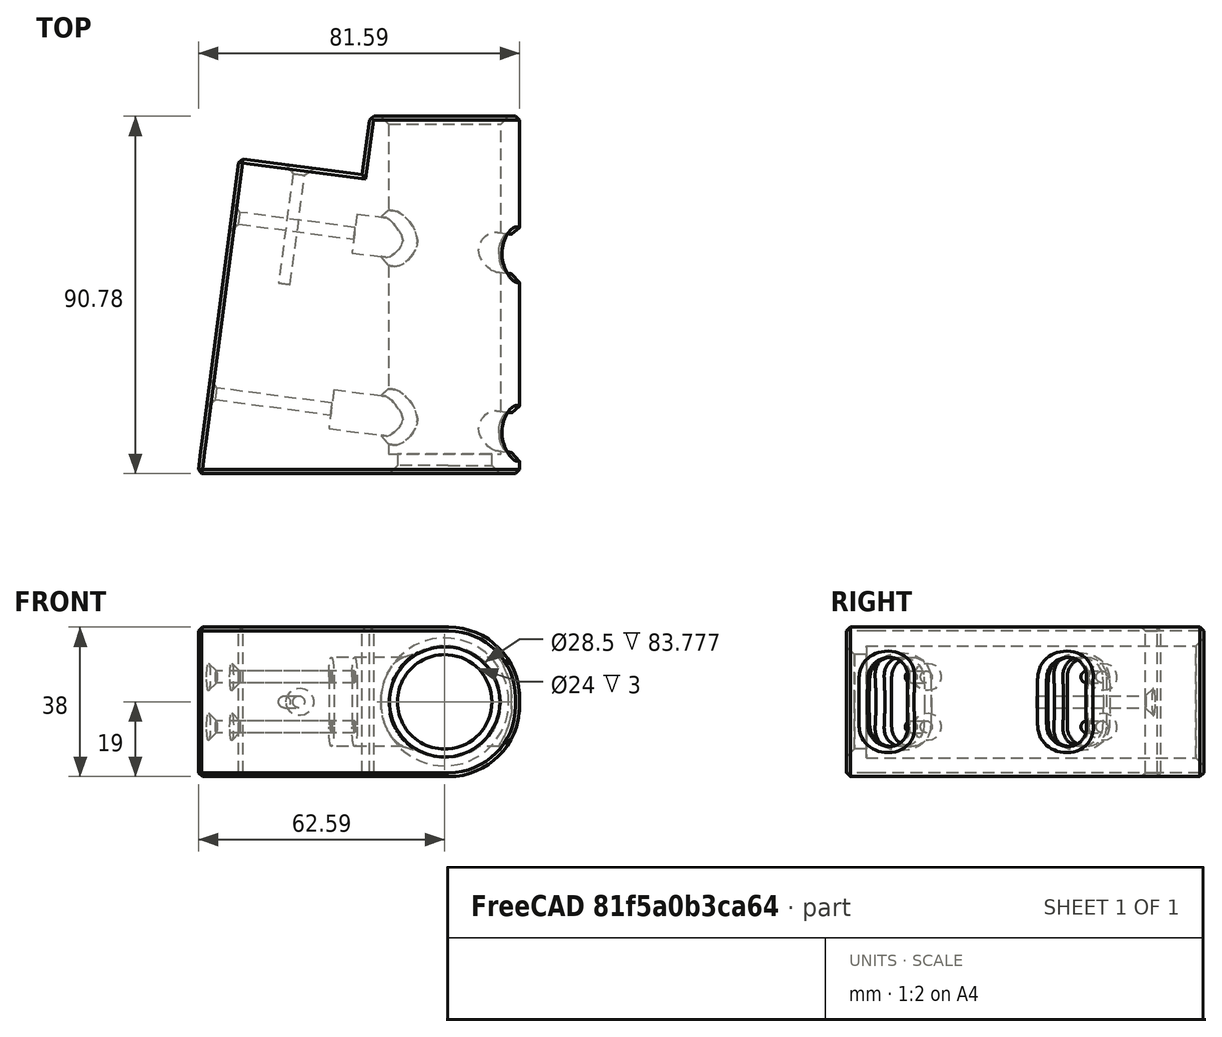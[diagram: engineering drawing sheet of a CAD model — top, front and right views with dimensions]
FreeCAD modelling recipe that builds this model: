
FCSTD DOCUMENT  (FreeCAD 0.18R16110 (Git))
Label: Support_mat_V2
License: All rights reserved
LicenseURL: http://en.wikipedia.org/wiki/All_rights_reserved
objects: PartDesign::Chamfer×9, Sketcher::SketchObject×8, PartDesign::Pocket×5, PartDesign::Pad×3, PartDesign::Fillet×1, PartDesign::Plane×1, PartDesign::Body×1, Mesh::Feature×1
note: 36 computed .brp shape members not serialized (recipe doc carries the construction recipe); baked Part::Feature solids carry a one-line shape summary decoded from their .brp

FEATURE [Sketcher::SketchObject] Sketch
  MapMode = 5
  Support = -> [XY_Plane]
  sketch-geometry (7):
    g0: LineSegment StartX=19 StartY=0 StartZ=0 EndX=-19 EndY=0 EndZ=0
    g1: LineSegment StartX=-61.9779 StartY=-85.1185 StartZ=0 EndX=-19 EndY=-90.7766 EndZ=0
    g2: LineSegment StartX=-19 StartY=-90.7766 StartZ=0 EndX=19 EndY=-90.7766 EndZ=0
    g3: LineSegment StartX=19 StartY=-90.7766 StartZ=0 EndX=19 EndY=0 EndZ=0
    g4: LineSegment StartX=-19 StartY=0 StartZ=0 EndX=-20.9579 EndY=-14.8717 EndZ=0
    g5: LineSegment StartX=-20.9579 StartY=-14.8717 StartZ=0 EndX=-52.1884 EndY=-10.7601 EndZ=0
    g6: LineSegment StartX=-52.1884 StartY=-10.7601 StartZ=0 EndX=-61.9779 EndY=-85.1185 EndZ=0
  constraints (20):
    c: PointOnObject(g0,g-1)
    c: Coincident(g1,g2)
    c: Horizontal(g2)
    c: Coincident(g2,g3)
    c: Coincident(g3,g0)
    c: Vertical(g3)
    c: Coincident(g0,g4)
    c: Coincident(g4,g5)
    c: Coincident(g5,g6)
    c: Coincident(g6,g1)
    c: Angle(g4,g0) = 1.7017
    c: Perpendicular(g4,g5)
    c: Perpendicular(g5,g6)
    c: Perpendicular(g1,g6)
    c: Distance(g5) = 31.5
    c: Distance(g4) = 15
    c: DistanceX(g0,g0) = 38
    c: Distance(g6) = 75
    c: Equal(g2,g0)
    c: Symmetric(g0,g0,g-2)
FEATURE [PartDesign::Pad] Pad
  Length = 38
  Length2 = 100
  Profile = -> Sketch
  Type = 0
FEATURE [Sketcher::SketchObject] Sketch001
  MapMode = 5
  Placement = pos=(0,0,0) rot=(0,0.707107,0.707107;3.14159rad)
  Support = -> [Pad]
  sketch-geometry (1):
    g0: Circle CenterX=0 CenterY=19 CenterZ=0 NormalX=0 NormalY=0 NormalZ=1 AngleXU=0 Radius=14.25
  constraints (3):
    c: Radius(g0) = 14.25
    c: Distance(g-1,g0) = 19
    c: PointOnObject(g0,g-2)
FEATURE [PartDesign::Pocket] Pocket
  BaseFeature = -> Pad
  Length = 100
  Length2 = 100
  Profile = -> Sketch001
  Type = 0
FEATURE [PartDesign::Fillet] Fillet
  Base = -> Pocket [Edge7,Edge8]
  BaseFeature = -> Pocket
  Radius = 18
FEATURE [Sketcher::SketchObject] Sketch002
  ExternalGeometry = -> [Fillet]
  MapMode = 5
  Placement = pos=(-49.9068,6.57036,0) rot=(-0.527011,0.600941,0.600941;4.11164rad)
  Support = -> [Fillet]
  sketch-geometry (4):
    g0: Circle CenterX=32.48 CenterY=25.3333 CenterZ=0 NormalX=0 NormalY=0 NormalZ=1 AngleXU=0 Radius=1.5
    g1: Circle CenterX=32.48 CenterY=12.6667 CenterZ=0 NormalX=0 NormalY=0 NormalZ=1 AngleXU=0 Radius=1.5
    g2: Circle CenterX=77.48 CenterY=25.3333 CenterZ=0 NormalX=0 NormalY=0 NormalZ=1 AngleXU=0 Radius=1.5
    g3: Circle CenterX=77.48 CenterY=12.6667 CenterZ=0 NormalX=0 NormalY=0 NormalZ=1 AngleXU=0 Radius=1.5
  constraints (12):
    c: Radius(g3) = 1.5
    c: Equal(g3,g2)
    c: Equal(g3,g0)
    c: Equal(g3,g1)
    c: Distance(g0,g-3) = 15
    c: Distance(g1,g-3) = 15
    c: Distance(g2,g-5) = 15
    c: Distance(g3,g-5) = 15
    c: DistanceY(g-1,g1) = 12.6667
    c: Distance(g0,g-4) = 12.6667
    c: Distance(g2,g-4) = 12.6667
    c: DistanceY(g-1,g3) = 12.6667
FEATURE [PartDesign::Pocket] Pocket001
  BaseFeature = -> Fillet
  Length = 100
  Length2 = 100
  Profile = -> Sketch002
  Type = 0
FEATURE [PartDesign::Plane] DatumPlane
  Length = 125.134
  MapMode = 5
  Placement = pos=(-18.6763,2.45878,0) rot=(-0.527011,0.600941,0.600941;4.11164rad)
  ResizeMode = 0
  Support = -> [Pocket001]
  Width = 62.57
FEATURE [Sketcher::SketchObject] Sketch003
  ExternalGeometry = -> [Pocket001]
  MapMode = 5
  Placement = pos=(-18.6763,2.45878,0) rot=(-0.527011,0.600941,0.600941;4.11164rad)
  Support = -> [DatumPlane]
  sketch-geometry (8):
    g0: ArcOfCircle CenterX=32.48 CenterY=25.3333 CenterZ=0 NormalX=0 NormalY=0 NormalZ=1 AngleXU=0 Radius=5 StartAngle=1.1e-15 EndAngle=3.14159
    g1: ArcOfCircle CenterX=32.48 CenterY=12.6667 CenterZ=0 NormalX=0 NormalY=0 NormalZ=1 AngleXU=0 Radius=5 StartAngle=3.14159 EndAngle=6.28319
    g2: LineSegment StartX=27.48 StartY=25.3333 StartZ=0 EndX=27.48 EndY=12.6667 EndZ=0
    g3: LineSegment StartX=37.48 StartY=25.3333 StartZ=0 EndX=37.48 EndY=12.6667 EndZ=0
    g4: ArcOfCircle CenterX=77.48 CenterY=25.3333 CenterZ=0 NormalX=0 NormalY=0 NormalZ=1 AngleXU=0 Radius=5 StartAngle=0 EndAngle=3.14159
    g5: ArcOfCircle CenterX=77.48 CenterY=12.6667 CenterZ=0 NormalX=0 NormalY=0 NormalZ=1 AngleXU=0 Radius=5 StartAngle=3.14159 EndAngle=6.28319
    g6: LineSegment StartX=72.48 StartY=25.3333 StartZ=0 EndX=72.48 EndY=12.6667 EndZ=0
    g7: LineSegment StartX=82.48 StartY=25.3333 StartZ=0 EndX=82.48 EndY=12.6667 EndZ=0
  constraints (16):
    c: Tangent(g0,g3) = 1.5708
    c: Tangent(g0,g2) = -1.5708
    c: Tangent(g2,g1) = -1.5708
    c: Tangent(g3,g1) = 1.5708
    c: Vertical(g2)
    c: Coincident(g0,g-3)
    c: Coincident(g1,g-4)
    c: Radius(g1) = 5
    c: Tangent(g4,g7) = 1.5708
    c: Tangent(g4,g6) = -1.5708
    c: Tangent(g6,g5) = -1.5708
    c: Tangent(g7,g5) = 1.5708
    c: Vertical(g6)
    c: Coincident(g4,g-5)
    c: Coincident(g5,g-6)
    c: Radius(g5) = 5
FEATURE [PartDesign::Pocket] Pocket002
  BaseFeature = -> Pocket001
  Length = 70
  Length2 = 100
  Profile = -> Sketch003
  Type = 0
FEATURE [Sketcher::SketchObject] Sketch004
  ExternalGeometry = -> [Pocket002,DatumPlane]
  MapMode = 5
  Placement = pos=(-2.2816,-17.3305,0) rot=(0.046297,0.706349,0.706349;3.04907rad)
  Support = -> [Pocket002]
  sketch-geometry (1):
    g0: Circle CenterX=34.8375 CenterY=19 CenterZ=0 NormalX=0 NormalY=0 NormalZ=1 AngleXU=0 Radius=1.5
  constraints (3):
    c: Radius(g0) = 1.5
    c: Distance(g0,g-3) = 19
    c: Distance(g0,g-4) = 15.5
FEATURE [PartDesign::Pocket] Pocket003
  BaseFeature = -> Pocket002
  Length = 30
  Length2 = 100
  Profile = -> Sketch004
  Type = 0
FEATURE [PartDesign::Chamfer] Chamfer
  Base = -> Pocket003 [Edge80,Edge82,Edge83,Edge85,Edge84]
  BaseFeature = -> Pocket003
  Size = 2
FEATURE [PartDesign::Chamfer] Chamfer001
  Base = -> Chamfer [Edge52,Edge48]
  BaseFeature = -> Chamfer
  Size = 2
FEATURE [PartDesign::Chamfer] Chamfer002
  Base = -> Chamfer001 [Edge70]
  BaseFeature = -> Chamfer001
  Size = 2
FEATURE [PartDesign::Chamfer] Chamfer003
  Base = -> Chamfer002 [Edge11]
  BaseFeature = -> Chamfer002
  Size = 2
FEATURE [PartDesign::Chamfer] Chamfer004
  Base = -> Chamfer003 [Edge11]
  BaseFeature = -> Chamfer003
  Size = 2
FEATURE [PartDesign::Chamfer] Chamfer005
  Base = -> Chamfer004 [Edge84]
  BaseFeature = -> Chamfer004
  Size = 1
FEATURE [Sketcher::SketchObject] Sketch006
  MapMode = 5
  Placement = pos=(0,0,38) rot=(0,0,1;0rad)
  sketch-geometry (3):
    g0: LineSegment StartX=1 StartY=-90.7766 StartZ=0 EndX=-61.6371 EndY=-82.5303 EndZ=0
    g1: LineSegment StartX=-61.6371 StartY=-82.5303 StartZ=0 EndX=-62.7228 EndY=-90.7766 EndZ=0
    g2: LineSegment StartX=-62.7228 StartY=-90.7766 StartZ=0 EndX=1 EndY=-90.7766 EndZ=0
  constraints (5):
    c: Coincident(g0,g1)
    c: Coincident(g1,g2)
    c: Coincident(g2,g0)
    c: Horizontal(g2)
    c: Perpendicular(g1,g0)
FEATURE [PartDesign::Pad] Pad002
  BaseFeature = -> Chamfer005
  Length = 38
  Length2 = 100
  Profile = -> Sketch006
  Reversed = true
  Type = 0
FEATURE [Sketcher::SketchObject] Sketch007
  MapMode = 5
  Placement = pos=(0,-90.7766,0) rot=(1,0,0;1.5708rad)
  Support = -> [Pad002]
  sketch-geometry (1):
    g0: Circle CenterX=0 CenterY=19 CenterZ=0 NormalX=0 NormalY=0 NormalZ=1 AngleXU=0 Radius=17
  constraints (3):
    c: PointOnObject(g0,g-2)
    c: Radius(g0) = 17
    c: DistanceY(g-1,g0) = 19
FEATURE [PartDesign::Pad] Pad003
  BaseFeature = -> Pad002
  Length = 5
  Length2 = 100
  Profile = -> Sketch007
  Reversed = true
  Type = 0
FEATURE [Sketcher::SketchObject] Sketch008
  ExternalGeometry = -> [Pad003]
  MapMode = 5
  Placement = pos=(0,-90.7766,0) rot=(1,0,0;1.5708rad)
  Support = -> [Pad003]
  sketch-geometry (1):
    g0: Circle CenterX=0 CenterY=19 CenterZ=0 NormalX=0 NormalY=0 NormalZ=1 AngleXU=0 Radius=12
  constraints (2):
    c: Coincident(g0,g-3)
    c: Radius(g0) = 12
FEATURE [PartDesign::Pocket] Pocket004
  BaseFeature = -> Pad003
  Length = 5
  Length2 = 100
  Profile = -> Sketch008
  Type = 0
FEATURE [PartDesign::Chamfer] Chamfer006
  Base = -> Pocket004 [Edge201]
  BaseFeature = -> Pocket004
  Size = 2
FEATURE [PartDesign::Chamfer] Chamfer007
  Base = -> Chamfer006 [Edge98,Edge194,Edge196,Edge193,Edge207,Edge197,Edge195,Edge175,Edge176]
  BaseFeature = -> Chamfer006
  Size = 1
FEATURE [PartDesign::Chamfer] Chamfer008
  Base = -> Chamfer007 [Edge167]
  BaseFeature = -> Chamfer007
  Size = 1
FEATURE [PartDesign::Body] Body
  Group = -> [Sketch,Pad,Sketch001,Pocket,Fillet,Sketch002,Pocket001,DatumPlane,Sketch003,Pocket002,Sketch004,Pocket003,Chamfer,Chamfer001,Chamfer002,Chamfer003,Chamfer004,Chamfer005,Sketch006,Pad002,Sketch007,Pad003,Sketch008,Pocket004,Chamfer006,Chamfer007,Chamfer008]
  Origin = -> Origin
  Tip = -> Chamfer008
FEATURE [Mesh::Feature] Mesh  label="Body (Meshed)"
